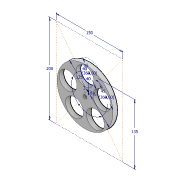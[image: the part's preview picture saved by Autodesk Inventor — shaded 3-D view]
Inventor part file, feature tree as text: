
AUTODESK INVENTOR PART (.ipt)
format: ipt  version: 2021 (Build 250183000, 183)  size: 127,488 bytes
history: native  units: mm
features: extrude x2, sketch x1, hole x1
ambient origin geometry x8: Origin, YZ Plane, XZ Plane, XY Plane, X Axis, Y Axis, Z Axis, Center Point
bodies: Solid1 (feature_tree)
feature tree (4):
  sketch  "Sketch1"  dims[d0=56.0mm d1=150.0mm d2=200.0mm d3=135.0mm d4=40.0mm d5=50.0mm d7=360.0deg d9=40.0mm d10=125.0mm d11=3.0mm d12=8.1mm d13=10.0mm d14=0.0mm d15=7.0mm d16=0.0mm d17=45.0mm d18=50.0mm d20=360.0deg d22=8.0mm d23=2.0mm d24=6.0mm d25=4.0mm d26=2.0mm d27=90.0deg d28=8.0mm d29=20.594885mm]
  extrude  "Extrusion1"  Depth=7.0mm
  extrude  "Extrusion2"  Depth=7.0mm
  hole  "Hole1"  [1 undecoded]
note: 1 required parameter value undecoded (feature->parameter linkage not recoverable at this tier; creation-order binding heuristic only, values carry confidence <= 0.55)
